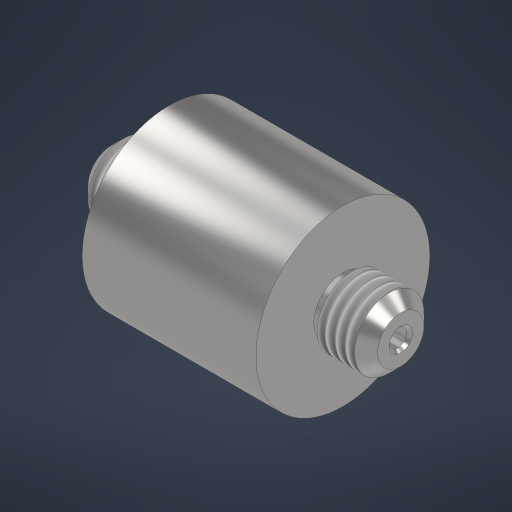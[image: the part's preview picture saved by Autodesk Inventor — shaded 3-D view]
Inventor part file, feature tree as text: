
AUTODESK INVENTOR PART (.ipt)
format: ipt  version: 2024.1 (Build 281209000, 209)  size: 309,760 bytes
history: native  units: mm
features: sketch x2, revolve x2, chamfer x2, thread x1, hole x1
ambient origin geometry x8: Origin, YZ Plane, XZ Plane, XY Plane, X Axis, Y Axis, Z Axis, Center Point
bodies: Solid1 (feature_tree)
feature tree (8):
  sketch  "Sketch1"  dims[d0=30.0mm d1=12.0mm]
  revolve  "Revolution1"  [1 undecoded]
  revolve  "Revolution2"  Angle=60.0deg
  thread  "Thread2"  [1 undecoded]
  chamfer  "Chamfer1"  Distance=30.0mm
  chamfer  "Chamfer2"  Distance=50.0mm
  hole  "Hole1"  [1 undecoded]
  sketch  "Sketch2"  dims[d3=8.42265mm d5=60.0deg d6=10.0mm d7=30.0mm d8=50.0mm d9=10.297443mm d10=10.0mm d11=3.0mm d12=18.0mm d13=23.0mm d14=360.0deg d15=90.0deg d18=50.0mm d19=0.0mm d20=2.0mm d21=2.0mm d22=45.0deg d23=3.0mm d24=0.5mm d25=2.0mm d26=45.0deg d27=10.0mm d29=1.0mm d30=10.106mm d31=16.0mm d32=13.0mm d33=2.0mm d34=90.0deg d35=20.0mm d36=20.594885mm]
note: 3 required parameter values undecoded (feature->parameter linkage not recoverable at this tier; creation-order binding heuristic only, values carry confidence <= 0.55)